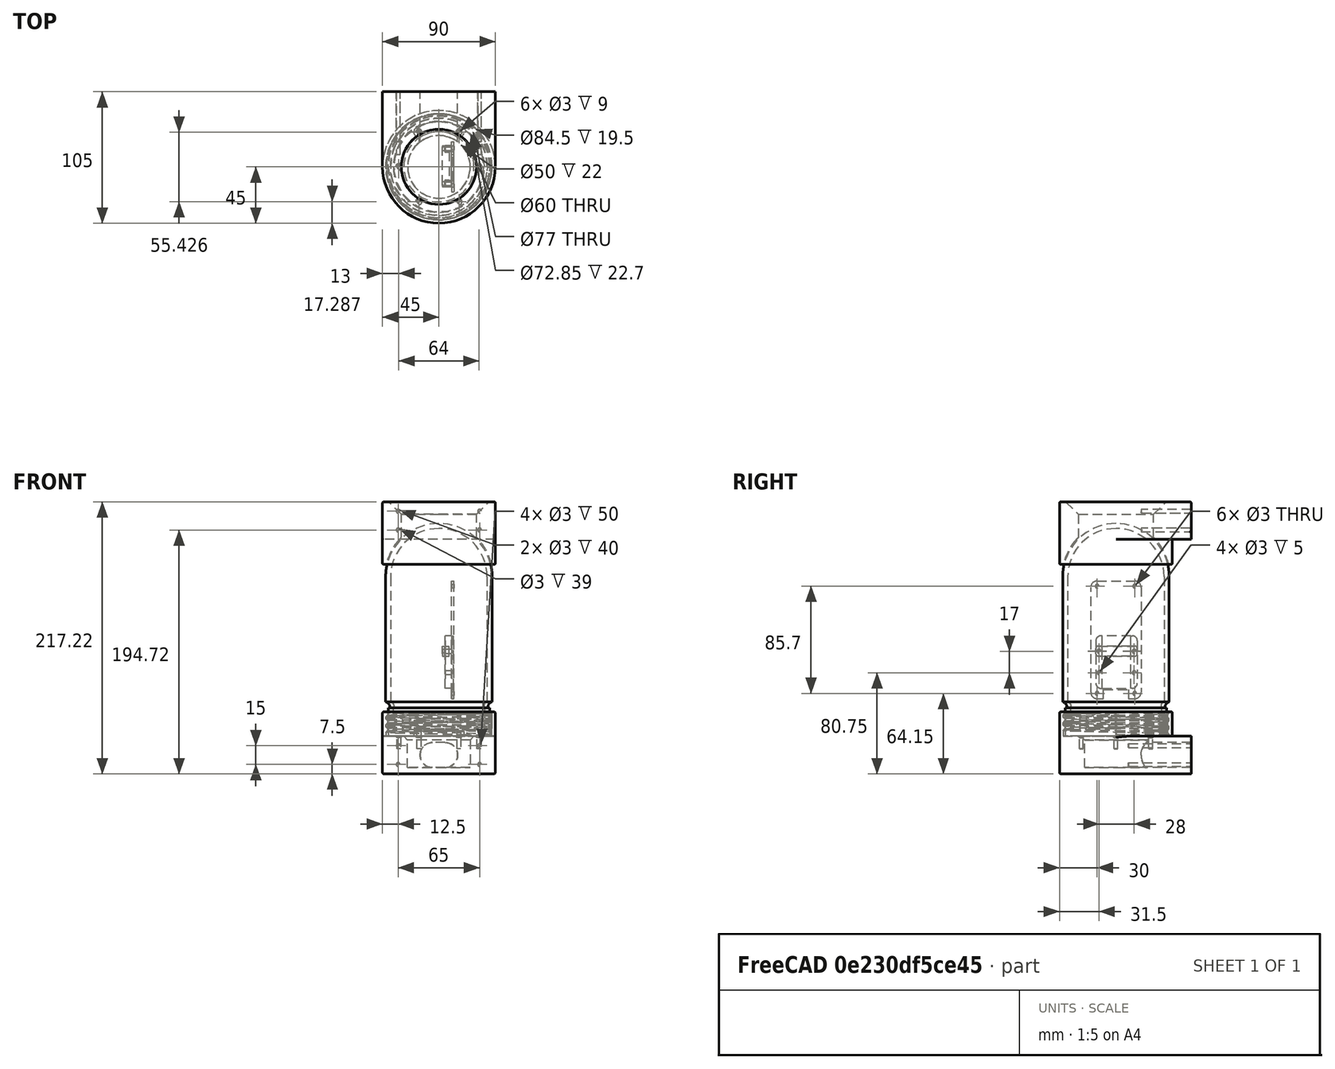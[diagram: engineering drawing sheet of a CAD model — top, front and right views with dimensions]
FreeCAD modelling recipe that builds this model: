
FCSTD DOCUMENT  (FreeCAD 0.19R)
Label: CrocSaintGerard_V4
License: All rights reserved
LicenseURL: http://en.wikipedia.org/wiki/All_rights_reserved
objects: Sketcher::SketchObject×31, PartDesign::Pocket×14, PartDesign::Pad×13, PartDesign::Fillet×11, PartDesign::Body×10, PartDesign::Chamfer×4, PartDesign::Revolution×2, Mesh::Feature×2, Part::Helix×1, PartDesign::ShapeBinder×1, PartDesign::AdditivePipe×1, PartDesign::LinearPattern×1, PartDesign::Groove×1, App::VRMLObject×1
note: 136 computed .brp shape members not serialized (recipe doc carries the construction recipe); baked Part::Feature solids carry a one-line shape summary decoded from their .brp

FEATURE [Part::Helix] Helix
  Angle = 0
  AttacherType = Attacher::AttachEngine3D
  Height = 6.22
  LocalCoord = 0
  Pitch = 6.23
  Radius = 40.5
  Style = 1
FEATURE [Sketcher::SketchObject] Sketch001  label="sketch_cylindre_base"
  FullyConstrained = true
  MapMode = 5
  Support = -> [XY_Plane]
  sketch-geometry (2):
    g0: Circle CenterX=0 CenterY=0 CenterZ=0 NormalX=0 NormalY=0 NormalZ=1 AngleXU=0 Radius=42.25
    g1: Circle CenterX=0 CenterY=0 CenterZ=0 NormalX=0 NormalY=0 NormalZ=1 AngleXU=0 Radius=45
  constraints (4):
    c: Coincident(g0,g-1)
    c: Coincident(g1,g0)
    c: Radius(g0) = 42.25
    c: Radius(g1) = 45
FEATURE [PartDesign::Pad] Pad  label="cylindre_base"
  Direction = (1,1,1)
  Length = 20
  Length2 = 100
  Profile = -> Sketch001
  Type = 0
FEATURE [Sketcher::SketchObject] Sketch002  label="sketch_profil_dent"
  FullyConstrained = true
  MapMode = 5
  Placement = pos=(0,0,0) rot=(1,0,0;1.5708rad)
  Support = -> [XZ_Plane]
  sketch-geometry (7):
    g0: LineSegment StartX=42.25 StartY=4.40427 StartZ=0 EndX=40.9557 EndY=3.11 EndZ=0
    g1: LineSegment StartX=40.9557 StartY=3.11 StartZ=0 EndX=40.9557 EndY=1.29427 EndZ=0
    g2: LineSegment StartX=40.9557 StartY=1.29427 StartZ=0 EndX=42.25 EndY=0 EndZ=0
    g3: LineSegment StartX=42.25 StartY=4.40427 StartZ=0 EndX=42.25 EndY=6.22 EndZ=0
    g4: LineSegment StartX=42.25 StartY=6.22 StartZ=0 EndX=43.25 EndY=6.22 EndZ=0
    g5: LineSegment StartX=43.25 StartY=6.22 StartZ=0 EndX=43.25 EndY=0 EndZ=0
    g6: LineSegment StartX=43.25 StartY=0 StartZ=0 EndX=42.25 EndY=0 EndZ=0
  constraints (21):
    c: Coincident(g0,g1)
    c: Vertical(g1)
    c: Coincident(g1,g2)
    c: DistanceX(g-2,g2) = 42.25
    c: PointOnObject(g2,g-1)
    c: Coincident(g0,g3)
    c: Vertical(g3)
    c: Coincident(g3,g4)
    c: Horizontal(g4)
    c: Coincident(g4,g5)
    c: PointOnObject(g5,g-1)
    c: Vertical(g5)
    c: Coincident(g5,g6)
    c: Coincident(g6,g2)
    c: DistanceX(g4,g4) = 1
    c: Equal(g3,g1)
    c: Equal(g2,g0)
    c: Angle(g2,g-1) = 0.785398
    c: Equal(g1,g3)
    c: DistanceY(g5,g5) = 6.22
    c: DistanceX(g-2,g0) = 42.25
FEATURE [PartDesign::ShapeBinder] ShapeBinder  label="ShapeBinder-helix"
  Support = -> [Helix]
  TraceSupport = false
FEATURE [PartDesign::AdditivePipe] AdditivePipe  label="filet"
  AuxilleryCurvelinear = true
  AuxillerySpineTangent = false
  BaseFeature = -> Pad
  Binormal = (0,0,0)
  Mode = 2
  Profile = -> Sketch002
  Spine = -> ShapeBinder
  SpineTangent = false
  Transformation = 0
  Transition = 0
FEATURE [PartDesign::LinearPattern] LinearPattern  label="ajout_filets"
  BaseFeature = -> AdditivePipe
  Direction = -> Z_Axis
  Length = 12.46
  Occurrences = 3
  Originals = -> [AdditivePipe]
FEATURE [Sketcher::SketchObject] Sketch003  label="sketch_decoupe_filetage"
  FullyConstrained = true
  MapMode = 5
  Placement = pos=(0,0,0) rot=(1,0,0;1.5708rad)
  Support = -> [XZ_Plane]
  sketch-geometry (4):
    g0: LineSegment StartX=-90 StartY=29.5 StartZ=0 EndX=90 EndY=29.5 EndZ=0
    g1: LineSegment StartX=90 StartY=29.5 StartZ=0 EndX=90 EndY=19.5 EndZ=0
    g2: LineSegment StartX=90 StartY=19.5 StartZ=0 EndX=-90 EndY=19.5 EndZ=0
    g3: LineSegment StartX=-90 StartY=19.5 StartZ=0 EndX=-90 EndY=29.5 EndZ=0
  constraints (11):
    c: Coincident(g0,g1)
    c: Coincident(g1,g2)
    c: Coincident(g2,g3)
    c: Coincident(g3,g0)
    c: Horizontal(g2)
    c: Vertical(g1)
    c: Vertical(g3)
    c: DistanceY(g-1,g1) = 19.5
    c: Symmetric(g0,g0,g-2)
    c: DistanceY(g1,g1) = 10
    c: DistanceX(g0,g0) = 180
FEATURE [PartDesign::Pocket] Pocket  label="decoupe_filetage"
  BaseFeature = -> LinearPattern
  Length = 200
  Length2 = 100
  Midplane = true
  Profile = -> Sketch003
  Type = 0
FEATURE [Sketcher::SketchObject] Sketch008  label="sketch_enceinte_verre"
  FullyConstrained = true
  MapMode = 5
  Support = -> [XY_Plane003]
  sketch-geometry (11):
    g0: ArcOfCircle CenterX=-127.4 CenterY=0 CenterZ=0 NormalX=0 NormalY=0 NormalZ=1 AngleXU=0 Radius=42.5 StartAngle=1.5708 EndAngle=3.14159
    g1: ArcOfCircle CenterX=-127.4 CenterY=0 CenterZ=0 NormalX=0 NormalY=0 NormalZ=1 AngleXU=0 Radius=38.5 StartAngle=1.5708 EndAngle=3.14159
    g2: LineSegment StartX=-127.4 StartY=38.5 StartZ=0 EndX=-27.4 EndY=38.5 EndZ=0
    g3: ArcOfCircle CenterX=-24.2871 CenterY=39.1905 CenterZ=0 NormalX=0 NormalY=0 NormalZ=1 AngleXU=0 Radius=3.18854 StartAngle=3.35987 EndAngle=5.2334
    g4: LineSegment StartX=-22.7 StartY=36.425 StartZ=0 EndX=0 EndY=36.425 EndZ=0
    g5: LineSegment StartX=-127.4 StartY=42.5 StartZ=0 EndX=-27.4 EndY=42.5 EndZ=0
    g6: ArcOfCircle CenterX=-22.7 CenterY=43.802 CenterZ=0 NormalX=0 NormalY=0 NormalZ=1 AngleXU=0 Radius=4.87701 StartAngle=3.41184 EndAngle=4.71239
    g7: LineSegment StartX=-22.7 StartY=38.925 StartZ=0 EndX=-22.7 EndY=40.425 EndZ=0
    g8: LineSegment StartX=-22.7 StartY=40.425 StartZ=0 EndX=0 EndY=40.425 EndZ=0
    g9: LineSegment StartX=0 StartY=40.425 StartZ=0 EndX=0 EndY=36.425 EndZ=0
    g10: LineSegment StartX=-165.9 StartY=4.7e-15 StartZ=0 EndX=-169.9 EndY=5.2e-15 EndZ=0
  constraints (35):
    c: PointOnObject(g0,g-1)
    c: PointOnObject(g0,g-1)
    c: Coincident(g1,g0)
    c: PointOnObject(g1,g-1)
    c: Angle(g1) = 1.5708
    c: Angle(g0) = 1.5708
    c: Tangent(g1,g2) = 1.5708
    c: Coincident(g3,g2)
    c: Coincident(g4,g3)
    c: PointOnObject(g4,g-2)
    c: Horizontal(g4)
    c: Coincident(g5,g0)
    c: Horizontal(g5)
    c: Coincident(g6,g5)
    c: Coincident(g6,g7)
    c: Coincident(g7,g8)
    c: PointOnObject(g8,g-2)
    c: Horizontal(g8)
    c: Coincident(g8,g9)
    c: Coincident(g9,g4)
    c: Coincident(g10,g0)
    c: DistanceX(g10,g10) = 4
    c: Radius(g0) = 42.5
    c: Coincident(g1,g10)
    c: DistanceY(g9,g9) = 4
    c: Perpendicular(g6,g7)
    c: Vertical(g7)
    c: DistanceY(g-1,g4) = 36.425
    c: Equal(g4,g8)
    c: DistanceX(g8,g8) = 22.7
    c: DistanceX(g-2,g5) = -27.4
    c: Equal(g2,g5)
    c: PointOnObject(g3,g6)
    c: DistanceY(g7,g7) = 1.5
    c: DistanceX(g5,g5) = 100
FEATURE [PartDesign::Revolution] Revolution  label="revolution_enceinte_verre"
  AllowMultiFace = false
  Angle = 360
  Axis = (1,0,0)
  Base = (0,0,0)
  Profile = -> Sketch008
  ReferenceAxis = -> Sketch008 [H_Axis]
FEATURE [PartDesign::Body] Body003  label="enceinte_verre"
  Group = -> [Sketch008,Revolution]
  Origin = -> Origin003
  Placement = pos=(-3.8e-15,0,-1.78e-14) rot=(0,1,0;1.5708rad)
  Tip = -> Revolution
FEATURE [Sketcher::SketchObject] Sketch  label="sketch_base"
  ExternalGeometry = -> [Pocket]
  FullyConstrained = true
  MapMode = 5
  Placement = pos=(0,0,0) rot=(1,0,0;3.14159rad)
  Support = -> [Pocket]
  sketch-geometry (4):
    g0: ArcOfCircle CenterX=0 CenterY=0 CenterZ=0 NormalX=0 NormalY=0 NormalZ=1 AngleXU=0 Radius=45 StartAngle=0 EndAngle=3.14159
    g1: LineSegment StartX=-45 StartY=5.5e-15 StartZ=0 EndX=-45 EndY=-60 EndZ=0
    g2: LineSegment StartX=-45 StartY=-60 StartZ=0 EndX=45 EndY=-60 EndZ=0
    g3: LineSegment StartX=45 StartY=-60 StartZ=0 EndX=45 EndY=0 EndZ=0
  constraints (11):
    c: Coincident(g0,g-1)
    c: PointOnObject(g0,g-1)
    c: PointOnObject(g0,g-1)
    c: Tangent(g0,g1) = -1.5708
    c: Coincident(g1,g2)
    c: Horizontal(g2)
    c: Coincident(g2,g3)
    c: Coincident(g3,g0)
    c: Vertical(g3)
    c: Radius(g0) = 45
    c: DistanceY(g1,g1) = 60
FEATURE [PartDesign::Pad] Pad001  label="base"
  BaseFeature = -> Pocket
  Direction = (1,1,1)
  Length = 30
  Length2 = 100
  Profile = -> Sketch
  Type = 0
FEATURE [Sketcher::SketchObject] Sketch009  label="sketch_passage_fils"
  FullyConstrained = true
  MapMode = 5
  Support = -> [Pad001]
  sketch-geometry (1):
    g0: Circle CenterX=0 CenterY=0 CenterZ=0 NormalX=0 NormalY=0 NormalZ=1 AngleXU=0 Radius=25
  constraints (2):
    c: Coincident(g0,g-1)
    c: Radius(g0) = 25
FEATURE [PartDesign::Pocket] Pocket001  label="passage_fils"
  BaseFeature = -> Pad001
  Length = 25
  Length2 = 100
  Profile = -> Sketch009
  Type = 0
FEATURE [Sketcher::SketchObject] Sketch010  label="sketch_passage_fils_vertical"
  ExternalGeometry = -> [Pocket001]
  FullyConstrained = true
  MapMode = 5
  Placement = pos=(0,60,0) rot=(0,0.707107,0.707107;3.14159rad)
  Support = -> [Pocket001]
  sketch-geometry (4):
    g0: ArcOfCircle CenterX=-5 CenterY=-15 CenterZ=0 NormalX=0 NormalY=0 NormalZ=1 AngleXU=0 Radius=10 StartAngle=1.5708 EndAngle=4.71239
    g1: ArcOfCircle CenterX=5 CenterY=-15 CenterZ=0 NormalX=0 NormalY=0 NormalZ=1 AngleXU=0 Radius=10 StartAngle=4.71239 EndAngle=7.85398
    g2: LineSegment StartX=-5 StartY=-25 StartZ=0 EndX=5 EndY=-25 EndZ=0
    g3: LineSegment StartX=-5 StartY=-5 StartZ=0 EndX=5 EndY=-5 EndZ=0
  constraints (9):
    c: Tangent(g0,g3) = 1.5708
    c: Tangent(g0,g2) = -1.5708
    c: Tangent(g2,g1) = -1.5708
    c: Tangent(g3,g1) = 1.5708
    c: Equal(g0,g1)
    c: Symmetric(g0,g1,g-2)
    c: Distance(g1,g-3) = 5
    c: DistanceY(g-1,g1) = -5
    c: DistanceX(g2,g2) = 10
FEATURE [PartDesign::Pocket] Pocket002  label="passage_fils_vertical"
  BaseFeature = -> Pocket001
  Length = 60
  Length2 = 100
  Profile = -> Sketch010
  Type = 0
FEATURE [Sketcher::SketchObject] Sketch011  label="sketch_vis_fixation"
  ExternalGeometry = -> [Pocket002]
  FullyConstrained = true
  MapMode = 5
  Placement = pos=(0,60,0) rot=(0,0.707107,0.707107;3.14159rad)
  Support = -> [Pocket002]
  sketch-geometry (4):
    g0: Circle CenterX=-32.5 CenterY=-7.5 CenterZ=0 NormalX=0 NormalY=0 NormalZ=1 AngleXU=0 Radius=1.5
    g1: Circle CenterX=32.5 CenterY=-7.5 CenterZ=0 NormalX=0 NormalY=0 NormalZ=1 AngleXU=0 Radius=1.5
    g2: Circle CenterX=-32.5 CenterY=-22.5 CenterZ=0 NormalX=0 NormalY=0 NormalZ=1 AngleXU=0 Radius=1.5
    g3: Circle CenterX=32.5 CenterY=-22.5 CenterZ=0 NormalX=0 NormalY=0 NormalZ=1 AngleXU=0 Radius=1.5
  constraints (10):
    c: Symmetric(g1,g0,g-2)
    c: DistanceY(g-1,g0) = -7.5
    c: Distance(g0,g1) = 65
    c: Radius(g0) = 1.5
    c: Equal(g0,g1)
    c: Symmetric(g3,g2,g-2)
    c: Radius(g2) = 1.5
    c: Equal(g2,g3)
    c: Distance(g3,g2) = 65
    c: Distance(g3,g-3) = 7.5
FEATURE [PartDesign::Pocket] Pocket003  label="vis_fixation"
  BaseFeature = -> Pocket002
  Length = 50
  Length2 = 100
  Profile = -> Sketch011
  Type = 0
FEATURE [PartDesign::Chamfer] Chamfer
  Angle = 45
  Base = -> Pocket003 [Edge95]
  BaseFeature = -> Pocket003
  ChamferType = 0
  FlipDirection = false
  Size = 3
  Size2 = 1
  SupportTransform = false
FEATURE [Sketcher::SketchObject] Sketch012  label="sketch_vis_montage_interieur"
  FullyConstrained = true
  MapMode = 5
  Support = -> [Chamfer]
  sketch-geometry (13):
    g0: LineSegment StartX=-16 StartY=27.7128 StartZ=0 EndX=-32 EndY=-3.3857e-12 EndZ=0
    g1: LineSegment StartX=-32 StartY=-3.3857e-12 StartZ=0 EndX=-16 EndY=-27.7128 EndZ=0
    g2: LineSegment StartX=-16 StartY=-27.7128 StartZ=0 EndX=16 EndY=-27.7128 EndZ=0
    g3: LineSegment StartX=16 StartY=-27.7128 StartZ=0 EndX=32 EndY=9.738e-12 EndZ=0
    g4: LineSegment StartX=32 StartY=9.738e-12 StartZ=0 EndX=16 EndY=27.7128 EndZ=0
    g5: LineSegment StartX=16 StartY=27.7128 StartZ=0 EndX=-16 EndY=27.7128 EndZ=0
    g6: Circle CenterX=0 CenterY=0 CenterZ=0 NormalX=0 NormalY=0 NormalZ=1 AngleXU=0 Radius=32
    g7: Circle CenterX=-16 CenterY=27.7128 CenterZ=0 NormalX=0 NormalY=0 NormalZ=1 AngleXU=0 Radius=1.5
    g8: Circle CenterX=16 CenterY=27.7128 CenterZ=0 NormalX=0 NormalY=0 NormalZ=1 AngleXU=0 Radius=1.5
    g9: Circle CenterX=-32 CenterY=-3.3857e-12 CenterZ=0 NormalX=0 NormalY=0 NormalZ=1 AngleXU=0 Radius=1.5
    g10: Circle CenterX=32 CenterY=9.738e-12 CenterZ=0 NormalX=0 NormalY=0 NormalZ=1 AngleXU=0 Radius=1.5
    g11: Circle CenterX=16 CenterY=-27.7128 CenterZ=0 NormalX=0 NormalY=0 NormalZ=1 AngleXU=0 Radius=1.5
    g12: Circle CenterX=-16 CenterY=-27.7128 CenterZ=0 NormalX=0 NormalY=0 NormalZ=1 AngleXU=0 Radius=1.5
  constraints (28):
    c: Coincident(g0,g1)
    c: Coincident(g1,g2)
    c: Coincident(g2,g3)
    c: Coincident(g3,g4)
    c: Coincident(g4,g5)
    c: Coincident(g5,g0)
    c: Equal(g0, g1-g5) x5
    c: PointOnObject(g0,g6)
    c: PointOnObject(g1,g6)
    c: PointOnObject(g2,g6)
    c: PointOnObject(g3,g6)
    c: PointOnObject(g4,g6)
    c: PointOnObject(g5,g6)
    c: Coincident(g6,g-1)
    c: Horizontal(g5)
    c: Radius(g6) = 32
    c: Coincident(g7,g0)
    c: Coincident(g8,g4)
    c: Coincident(g9,g0)
    c: Coincident(g10,g3)
    c: Coincident(g11,g2)
    c: Coincident(g12,g1)
    c: Radius(g11) = 1.5
    c: Equal(g11,g12)
    c: Equal(g11,g9)
    c: Equal(g11,g7)
    c: Equal(g11,g8)
    c: Equal(g11,g10)
FEATURE [PartDesign::Pocket] Pocket004  label="vis_montage_interieur"
  BaseFeature = -> Chamfer
  Length = 10
  Length2 = 100
  Profile = -> Sketch012
  Type = 0
FEATURE [PartDesign::Chamfer] Chamfer001
  Angle = 45
  Base = -> Pocket004 [Edge3,Edge2,Edge4,Edge6,Edge8,Edge7]
  BaseFeature = -> Pocket004
  ChamferType = 0
  FlipDirection = false
  Size = 1
  Size2 = 1
  SupportTransform = false
FEATURE [Mesh::Feature] Mesh  label="fixation_enceinte_verre (Meshed)"
FEATURE [Sketcher::SketchObject] Sketch013
  FullyConstrained = true
  MapMode = 5
  Placement = pos=(0,0,0) rot=(0.57735,0.57735,0.57735;2.0944rad)
  Support = -> [YZ_Plane004]
  sketch-geometry (4):
    g0: ArcOfCircle CenterX=0 CenterY=128 CenterZ=0 NormalX=0 NormalY=0 NormalZ=1 AngleXU=0 Radius=43 StartAngle=2.39448 EndAngle=2.92551
    g1: LineSegment StartX=-42 StartY=137.22 StartZ=0 EndX=-45 EndY=137.22 EndZ=0
    g2: LineSegment StartX=-45 StartY=137.22 StartZ=0 EndX=-45 EndY=157.22 EndZ=0
    g3: LineSegment StartX=-45 StartY=157.22 StartZ=0 EndX=-31.5471 EndY=157.22 EndZ=0
  constraints (13):
    c: PointOnObject(g0,g-2)
    c: Coincident(g0,g1)
    c: Coincident(g1,g2)
    c: Vertical(g2)
    c: Coincident(g2,g3)
    c: Coincident(g3,g0)
    c: Horizontal(g3)
    c: Horizontal(g1)
    c: Radius(g0) = 43
    c: DistanceY(g2,g2) = 20
    c: DistanceX(g-2,g1) = -45
    c: DistanceY(g-1,g0) = 128
    c: DistanceX(g1,g1) = 3
FEATURE [PartDesign::Revolution] Revolution001
  Angle = 360
  Axis = (-2e-16,3e-16,1)
  Base = (0,0,0)
  Placement = pos=(0,0,0) rot=(0.57735,0.57735,0.57735;2.0944rad)
  Profile = -> Sketch013
  ReferenceAxis = -> Sketch013 [V_Axis]
FEATURE [Sketcher::SketchObject] Sketch014
  ExternalGeometry = -> [Revolution001]
  FullyConstrained = true
  MapMode = 5
  Placement = pos=(-8.73e-14,6.11e-14,157.22) rot=(0,0,-1;1.5708rad)
  Support = -> [Revolution001]
  sketch-geometry (4):
    g0: ArcOfCircle CenterX=0 CenterY=0 CenterZ=0 NormalX=0 NormalY=0 NormalZ=1 AngleXU=0 Radius=45 StartAngle=4.71239 EndAngle=7.85398
    g1: LineSegment StartX=1.38e-14 StartY=45 StartZ=0 EndX=-60 EndY=45 EndZ=0
    g2: LineSegment StartX=-60 StartY=45 StartZ=0 EndX=-60 EndY=-45 EndZ=0
    g3: LineSegment StartX=-60 StartY=-45 StartZ=0 EndX=-7.1e-15 EndY=-45 EndZ=0
  constraints (10):
    c: Coincident(g0,g-1)
    c: PointOnObject(g0,g-3)
    c: PointOnObject(g0,g-2)
    c: PointOnObject(g0,g-2)
    c: Tangent(g0,g1) = -1.5708
    c: Coincident(g1,g2)
    c: Coincident(g2,g3)
    c: Coincident(g3,g0)
    c: Symmetric(g2,g1,g-1)
    c: DistanceX(g-2,g1) = -60
FEATURE [PartDesign::Pad] Pad002
  BaseFeature = -> Revolution001
  Direction = (1,1,1)
  Length = 30
  Length2 = 100
  Placement = pos=(0,0,0) rot=(0.57735,0.57735,0.57735;2.0944rad)
  Profile = -> Sketch014
  Type = 0
FEATURE [Sketcher::SketchObject] Sketch015
  ExternalGeometry = -> [Pad002]
  FullyConstrained = true
  MapMode = 5
  Placement = pos=(0,0,0) rot=(0.57735,0.57735,0.57735;2.0944rad)
  Support = -> [YZ_Plane004]
  sketch-geometry (3):
    g0: ArcOfCircle CenterX=2.84e-14 CenterY=128 CenterZ=0 NormalX=0 NormalY=0 NormalZ=1 AngleXU=0 Radius=43 StartAngle=1.5708 EndAngle=2.39448
    g1: LineSegment StartX=-31.5471 StartY=157.22 StartZ=0 EndX=3.6e-15 EndY=157.22 EndZ=0
    g2: LineSegment StartX=3.6e-15 StartY=157.22 StartZ=0 EndX=3.6e-15 EndY=171 EndZ=0
  constraints (8):
    c: Coincident(g0,g-3)
    c: Coincident(g0,g-3)
    c: PointOnObject(g0,g-2)
    c: Coincident(g0,g1)
    c: Coincident(g1,g2)
    c: Coincident(g2,g0)
    c: Vertical(g2)
    c: Horizontal(g1)
FEATURE [PartDesign::Groove] Groove
  Angle = 360
  Axis = (-2e-16,3e-16,1)
  Base = (0,0,0)
  BaseFeature = -> Pad002
  Placement = pos=(0,0,0) rot=(0.57735,0.57735,0.57735;2.0944rad)
  Profile = -> Sketch015
  ReferenceAxis = -> Sketch015 [V_Axis]
  Reversed = true
FEATURE [PartDesign::Fillet] Fillet
  Base = -> Chamfer001 [Edge116,Edge168,Edge182,Edge171,Edge181,Edge166]
  BaseFeature = -> Chamfer001
  Radius = 1
  SupportTransform = false
FEATURE [PartDesign::Body] Body  label="fixation_enceinte_verre"
  Group = -> [Sketch001,Pad,Sketch002,ShapeBinder,AdditivePipe,LinearPattern,Sketch003,Pocket,Sketch,Pad001,Sketch009,Pocket001,Sketch010,Pocket002,Sketch011,Pocket003,Chamfer,Sketch012,Pocket004,Chamfer001,Fillet]
  Origin = -> Origin
  Tip = -> Fillet
FEATURE [Sketcher::SketchObject] Sketch019
  FullyConstrained = true
  MapMode = 5
  Support = -> [XY_Plane005]
  sketch-geometry (4):
    g0: ArcOfCircle CenterX=-1.9e-15 CenterY=0 CenterZ=0 NormalX=0 NormalY=0 NormalZ=1 AngleXU=0 Radius=28 StartAngle=1.0472 EndAngle=2.0944
    g1: ArcOfCircle CenterX=-1.9e-15 CenterY=0 CenterZ=0 NormalX=0 NormalY=0 NormalZ=1 AngleXU=0 Radius=36 StartAngle=1.0472 EndAngle=2.0944
    g2: ArcOfCircle CenterX=-16 CenterY=27.7128 CenterZ=0 NormalX=0 NormalY=0 NormalZ=1 AngleXU=0 Radius=4 StartAngle=2.0944 EndAngle=5.23599
    g3: ArcOfCircle CenterX=16 CenterY=27.7128 CenterZ=0 NormalX=0 NormalY=0 NormalZ=1 AngleXU=0 Radius=4 StartAngle=4.18879 EndAngle=7.33038
  constraints (11):
    c: Symmetric(g0,g0,g-2)
    c: Coincident(g1,g0)
    c: Symmetric(g1,g1,g-2)
    c: Coincident(g3,g1)
    c: Tangent(g2,g0) = 1.5708
    c: Tangent(g2,g1) = -1.5708
    c: Tangent(g3,g0) = 1.5708
    c: Coincident(g0,g-1)
    c: Radius(g1) = 36
    c: Radius(g0) = 28
    c: Angle(g0) = 1.0472
FEATURE [PartDesign::Pad] Pad003
  Direction = (1,1,1)
  Length = 4
  Length2 = 100
  Profile = -> Sketch019
  Type = 0
FEATURE [Sketcher::SketchObject] Sketch020
  ExternalGeometry = -> [Pad003]
  FullyConstrained = true
  MapMode = 5
  Placement = pos=(0,0,4) rot=(0,0,1;0rad)
  Support = -> [Pad003]
  sketch-geometry (2):
    g0: Circle CenterX=-16 CenterY=27.7128 CenterZ=0 NormalX=0 NormalY=0 NormalZ=1 AngleXU=0 Radius=1.5
    g1: Circle CenterX=16 CenterY=27.7128 CenterZ=0 NormalX=0 NormalY=0 NormalZ=1 AngleXU=0 Radius=1.5
  constraints (4):
    c: Coincident(g0,g-3)
    c: Coincident(g1,g-4)
    c: Radius(g1) = 1.5
    c: Equal(g1,g0)
FEATURE [PartDesign::Pocket] Pocket008
  BaseFeature = -> Pad003
  Length = 5
  Length2 = 100
  Profile = -> Sketch020
  Type = 0
FEATURE [PartDesign::Body] Body005  label="support_interieur"
  Group = -> [Sketch019,Pad003,Sketch020,Pocket008]
  Origin = -> Origin005
  Tip = -> Pocket008
FEATURE [Sketcher::SketchObject] Sketch021
  FullyConstrained = true
  MapMode = 5
  Placement = pos=(-1.806e-13,1.028e-13,187.22) rot=(0,0,-1;1.5708rad)
  Support = -> [Pad002]
  sketch-geometry (1):
    g0: Circle CenterX=0 CenterY=0 CenterZ=0 NormalX=0 NormalY=0 NormalZ=1 AngleXU=0 Radius=30
  constraints (2):
    c: Coincident(g0,g-1)
    c: Radius(g0) = 30
FEATURE [PartDesign::Pocket] Pocket009
  BaseFeature = -> Groove
  Length = 46
  Length2 = 100
  Placement = pos=(0,0,0) rot=(0.57735,0.57735,0.57735;2.0944rad)
  Profile = -> Sketch021
  Type = 0
FEATURE [Sketcher::SketchObject] Sketch022
  FullyConstrained = false
  MapMode = 5
  Placement = pos=(2.66e-14,60,-6.99e-14) rot=(0.57735,0.57735,0.57735;4.18879rad)
  sketch-geometry (4):
    g0: Circle CenterX=164.72 CenterY=32.5 CenterZ=0 NormalX=0 NormalY=0 NormalZ=1 AngleXU=0 Radius=1.5
    g1: Circle CenterX=179.72 CenterY=32.5 CenterZ=0 NormalX=0 NormalY=0 NormalZ=1 AngleXU=0 Radius=1.5
    g2: Circle CenterX=164.72 CenterY=-32.5 CenterZ=0 NormalX=0 NormalY=0 NormalZ=1 AngleXU=0 Radius=1.5
    g3: Circle CenterX=179.72 CenterY=-32.5 CenterZ=0 NormalX=0 NormalY=0 NormalZ=1 AngleXU=0 Radius=1.5
  constraints (8):
    c: Symmetric(g3,g1,g-1)
    c: Symmetric(g0,g2,g-1)
    c: Distance(g0,g2) = 65
    c: Distance(g3,g1) = 65
    c: Radius(g0) = 1.5
    c: Equal(g0,g1)
    c: Equal(g0,g2)
    c: Equal(g0,g3)
FEATURE [PartDesign::Pocket] Pocket010
  BaseFeature = -> Pocket009
  Length = 40
  Length2 = 100
  Placement = pos=(0,0,0) rot=(0.57735,0.57735,0.57735;2.0944rad)
  Profile = -> Sketch022
  Type = 0
FEATURE [PartDesign::Fillet] Fillet001
  Base = -> Pocket010 [Edge10,Edge27]
  BaseFeature = -> Pocket010
  Placement = pos=(0,0,0) rot=(0.57735,0.57735,0.57735;2.0944rad)
  Radius = 1
  SupportTransform = false
FEATURE [PartDesign::Fillet] Fillet002
  Base = -> Fillet001 [Edge5,Edge21]
  BaseFeature = -> Fillet001
  Placement = pos=(0,0,0) rot=(0.57735,0.57735,0.57735;2.0944rad)
  Radius = 1
  SupportTransform = false
FEATURE [PartDesign::Chamfer] Chamfer002
  Angle = 45
  Base = -> Fillet002 [Edge19]
  BaseFeature = -> Fillet002
  ChamferType = 0
  FlipDirection = false
  Placement = pos=(0,0,0) rot=(0.57735,0.57735,0.57735;2.0944rad)
  Size = 10
  Size2 = 1
  SupportTransform = false
FEATURE [PartDesign::Fillet] Fillet003
  Base = -> Chamfer002 [Edge2]
  BaseFeature = -> Chamfer002
  Placement = pos=(0,0,0) rot=(0.57735,0.57735,0.57735;2.0944rad)
  Radius = 1
  SupportTransform = false
FEATURE [PartDesign::Fillet] Fillet004
  Base = -> Fillet003 [Edge46,Edge5,Edge34]
  BaseFeature = -> Fillet003
  Placement = pos=(0,0,0) rot=(0.57735,0.57735,0.57735;2.0944rad)
  Radius = 1
  SupportTransform = false
FEATURE [PartDesign::Body] Body004  label="tete"
  Group = -> [Sketch013,Revolution001,Sketch014,Pad002,Sketch015,Groove,Sketch021,Pocket009,Sketch022,Pocket010,Fillet001,Fillet002,Chamfer002,Fillet003,Fillet004]
  Origin = -> Origin004
  Tip = -> Fillet004
FEATURE [Mesh::Feature] Mesh001  label="tete (Meshed)"
FEATURE [Sketcher::SketchObject] Sketch005
  FullyConstrained = false
  MapMode = 5
  Placement = pos=(0,0,0) rot=(0.57735,0.57735,0.57735;2.0944rad)
  Support = -> [YZ_Plane002]
  sketch-geometry (8):
    g0: LineSegment StartX=-17 StartY=-5 StartZ=0 EndX=-11.875 EndY=-5 EndZ=0
    g1: LineSegment StartX=-11.875 StartY=-5 StartZ=0 EndX=-11.875 EndY=-1.6 EndZ=0
    g2: LineSegment StartX=-11.875 StartY=-1.6 StartZ=0 EndX=10.875 EndY=-1.6 EndZ=0
    g3: LineSegment StartX=10.875 StartY=-1.6 StartZ=0 EndX=10.875 EndY=-5 EndZ=0
    g4: LineSegment StartX=10.875 StartY=-5 StartZ=0 EndX=16 EndY=-5 EndZ=0
    g5: LineSegment StartX=16 StartY=-5 StartZ=0 EndX=16 EndY=-7 EndZ=0
    g6: LineSegment StartX=16 StartY=-7 StartZ=0 EndX=-17 EndY=-7 EndZ=0
    g7: LineSegment StartX=-17 StartY=-7 StartZ=0 EndX=-17 EndY=-5 EndZ=0
  constraints (24):
    c: Horizontal(g0)
    c: Coincident(g0,g1)
    c: Vertical(g1)
    c: Coincident(g1,g2)
    c: Horizontal(g2)
    c: Coincident(g2,g3)
    c: Vertical(g3)
    c: Coincident(g3,g4)
    c: Horizontal(g4)
    c: Coincident(g4,g5)
    c: Vertical(g5)
    c: Coincident(g5,g6)
    c: Horizontal(g6)
    c: Coincident(g6,g7)
    c: Coincident(g7,g0)
    c: Vertical(g7)
    c: DistanceY(g7,g7) = 2
    c: DistanceY(g1,g1) = 3.4
    c: DistanceX(g2,g2) = 22.75
    c: DistanceX(g0,g0) = 5.125
    c: Equal(g0,g4)
    c: Equal(g5,g7)
    c: DistanceY(g-1,g0) = -5
    c: DistanceX(g-2,g6) = -17
FEATURE [PartDesign::Pad] Pad010
  AllowMultiFace = false
  Direction = (1,1,1)
  Length = 8
  Length2 = 100
  Placement = pos=(0,0,0) rot=(0.57735,0.57735,0.57735;2.0944rad)
  Profile = -> Sketch005
  Type = 0
FEATURE [Sketcher::SketchObject] Sketch006
  ExternalGeometry = -> [Pad010]
  FullyConstrained = true
  MapMode = 5
  Placement = pos=(2.7e-15,-3.9e-15,-7) rot=(0.707107,0.707107,0;3.14159rad)
  Support = -> [Pad010]
  sketch-geometry (2):
    g0: Circle CenterX=-14.5 CenterY=4 CenterZ=0 NormalX=0 NormalY=0 NormalZ=1 AngleXU=0 Radius=1.5
    g1: Circle CenterX=13.5 CenterY=4 CenterZ=0 NormalX=0 NormalY=0 NormalZ=1 AngleXU=0 Radius=1.5
  constraints (6):
    c: Radius(g1) = 1.5
    c: Equal(g1,g0)
    c: DistanceY(g-1,g1) = 4
    c: DistanceY(g-1,g0) = 4
    c: Distance(g0,g-3) = 2.5
    c: Distance(g1,g-4) = 2.5
FEATURE [PartDesign::Pocket] Pocket013
  AllowMultiFace = false
  BaseFeature = -> Pad010
  Length = 5
  Length2 = 100
  Placement = pos=(0,0,0) rot=(0.57735,0.57735,0.57735;2.0944rad)
  Profile = -> Sketch006
  Type = 0
FEATURE [PartDesign::Fillet] Fillet007
  Base = -> Pocket013 [Edge8,Edge7,Edge19,Edge13]
  BaseFeature = -> Pocket013
  Placement = pos=(0,0,0) rot=(0.57735,0.57735,0.57735;2.0944rad)
  Radius = 2
  SupportTransform = false
FEATURE [PartDesign::Body] Body002  label="Attache"
  Group = -> [Sketch005,Pad010,Sketch006,Pocket013,Fillet007]
  Origin = -> Origin002
  Placement = pos=(9.75,-3.1e-15,64) rot=(-0.707107,0,-0.707107;3.14159rad)
  Tip = -> Fillet007
FEATURE [App::VRMLObject] CroqueLivreSaintGerard2021_V1
  Placement = pos=(0,0,0) rot=(1,0,0;3.14159rad)
  Resources = CroqueLivreSaintGerard2021_V1/CP_Radial_D12.5mm_P5.00mm.wrl | CroqueLivreSaintGerard2021_V1/ | CroqueLivreSaintGerard2021_V1/ | CroqueLivreSaintGerard2021_V1/ | CroqueLivreSaintGerard2021_V1/ | CroqueLivreSaintGerard2021_V1/ | CroqueLivreSaintGerard2021_V1/ | CroqueLivreSaintGerard2021_V1/ | CroqueLivreSaintGerard2021_V1/ | CroqueLivreSaintGerard2021_V1/ | CroqueLivreSaintGerard2021_V1/ | CroqueLivreSaintGerard2021_V1/
FEATURE [Sketcher::SketchObject] Sketch025
  FullyConstrained = true
  MapMode = 5
  Support = -> [XY_Plane006]
  sketch-geometry (17):
    g0: LineSegment StartX=-47 StartY=20 StartZ=0 EndX=47 EndY=20 EndZ=0
    g1: LineSegment StartX=47 StartY=20 StartZ=0 EndX=47 EndY=-20 EndZ=0
    g2: LineSegment StartX=47 StartY=-20 StartZ=0 EndX=-47 EndY=-20 EndZ=0
    g3: LineSegment StartX=-39.75 StartY=18.75 StartZ=0 EndX=39.75 EndY=18.75 EndZ=0
    g4: LineSegment StartX=39.75 StartY=18.75 StartZ=0 EndX=39.75 EndY=-18.75 EndZ=0
    g5: LineSegment StartX=39.75 StartY=-18.75 StartZ=0 EndX=-39.75 EndY=-18.75 EndZ=0
    g6: LineSegment StartX=-39.75 StartY=-18.75 StartZ=0 EndX=-39.75 EndY=18.75 EndZ=0
    g7: Circle CenterX=-42.85 CenterY=15 CenterZ=0 NormalX=0 NormalY=0 NormalZ=1 AngleXU=0 Radius=1.5
    g8: Circle CenterX=-42.85 CenterY=-15 CenterZ=0 NormalX=0 NormalY=0 NormalZ=1 AngleXU=0 Radius=1.5
    g9: Circle CenterX=42.85 CenterY=-15 CenterZ=0 NormalX=0 NormalY=0 NormalZ=1 AngleXU=0 Radius=1.5
    g10: Circle CenterX=42.85 CenterY=15 CenterZ=0 NormalX=0 NormalY=0 NormalZ=1 AngleXU=0 Radius=1.5
    g11: Circle CenterX=-42.85 CenterY=15 CenterZ=0 NormalX=0 NormalY=0 NormalZ=1 AngleXU=0 Radius=3
    g12: LineSegment StartX=-47 StartY=20 StartZ=0 EndX=-47 EndY=10 EndZ=0
    g13: LineSegment StartX=-47 StartY=10 StartZ=0 EndX=-39.75 EndY=10 EndZ=0
    g14: LineSegment StartX=-39.75 StartY=10 StartZ=0 EndX=-39.75 EndY=-10 EndZ=0
    g15: LineSegment StartX=-39.75 StartY=-10 StartZ=0 EndX=-47 EndY=-10 EndZ=0
    g16: LineSegment StartX=-47 StartY=-10 StartZ=0 EndX=-47 EndY=-20 EndZ=0
  constraints (44):
    c: Coincident(g0,g1)
    c: Coincident(g1,g2)
    c: Horizontal(g0)
    c: Horizontal(g2)
    c: Vertical(g1)
    c: Symmetric(g0,g1,g-1)
    c: DistanceY(g1,g1) = 40
    c: DistanceX(g0,g0) = 94
    c: Coincident(g3,g4)
    c: Coincident(g4,g5)
    c: Coincident(g5,g6)
    c: Coincident(g6,g3)
    c: Horizontal(g3)
    c: Horizontal(g5)
    c: Vertical(g4)
    c: Vertical(g6)
    c: Symmetric(g3,g4,g-1)
    c: DistanceY(g6,g6) = 37.5
    c: DistanceX(g3,g3) = 79.5
    c: Radius(g10) = 1.5
    c: Equal(g10,g9)
    c: Equal(g10,g8)
    c: Equal(g10,g7)
    c: Symmetric(g7,g8,g-1)
    c: Symmetric(g10,g9,g-1)
    c: Symmetric(g10,g7,g-2)
    c: Coincident(g11,g7)
    c: Radius(g11) = 3
    c: Coincident(g0,g12)
    c: Vertical(g12)
    c: Coincident(g12,g13)
    c: Horizontal(g13)
    c: Coincident(g13,g14)
    c: Vertical(g14)
    c: Coincident(g14,g15)
    c: Horizontal(g15)
    c: Coincident(g15,g16)
    c: Coincident(g16,g2)
    c: Vertical(g16)
    c: Symmetric(g15,g12,g-1)
    c: PointOnObject(g13,g6)
    c: DistanceY(g14,g14) = 20
    c: DistanceY(g-1,g7) = 15
    c: DistanceX(g-2,g7) = -42.85
FEATURE [PartDesign::Pad] Pad011
  AllowMultiFace = false
  Direction = (1,1,1)
  Length = 2
  Length2 = 100
  Profile = -> Sketch025
  Type = 0
FEATURE [PartDesign::Fillet] Fillet006
  Base = -> Pad011 [Edge8,Edge5,Edge11,Edge1]
  BaseFeature = -> Pad011
  Radius = 5
  SupportTransform = false
FEATURE [Sketcher::SketchObject] Sketch024
  ExternalGeometry = -> [Fillet006]
  FullyConstrained = true
  MapMode = 5
  Placement = pos=(0,0,0) rot=(1,0,0;3.14159rad)
  Support = -> [Fillet006]
  sketch-geometry (4):
    g0: LineSegment StartX=-38.75 StartY=12 StartZ=0 EndX=3.25 EndY=12 EndZ=0
    g1: LineSegment StartX=3.25 StartY=12 StartZ=0 EndX=3.25 EndY=-11 EndZ=0
    g2: LineSegment StartX=3.25 StartY=-11 StartZ=0 EndX=-38.75 EndY=-11 EndZ=0
    g3: LineSegment StartX=-38.75 StartY=-11 StartZ=0 EndX=-38.75 EndY=12 EndZ=0
  constraints (12):
    c: Coincident(g0,g1)
    c: Coincident(g1,g2)
    c: Coincident(g2,g3)
    c: Coincident(g3,g0)
    c: Horizontal(g0)
    c: Horizontal(g2)
    c: Vertical(g1)
    c: Vertical(g3)
    c: DistanceY(g1,g1) = 23
    c: DistanceX(g0,g0) = 42
    c: DistanceY(g-1,g0) = 12
    c: Distance(g0,g-3) = 1
FEATURE [PartDesign::Pocket] Pocket012
  AllowMultiFace = false
  BaseFeature = -> Fillet006
  Length = 1.5
  Length2 = 100
  Profile = -> Sketch024
  Type = 0
FEATURE [Sketcher::SketchObject] Sketch026
  FullyConstrained = true
  MapMode = 5
  Support = -> [XY_Plane001]
  sketch-geometry (16):
    g0: LineSegment StartX=-47 StartY=20 StartZ=0 EndX=47 EndY=20 EndZ=0
    g1: LineSegment StartX=47 StartY=20 StartZ=0 EndX=47 EndY=-20 EndZ=0
    g2: LineSegment StartX=47 StartY=-20 StartZ=0 EndX=-47 EndY=-20 EndZ=0
    g3: LineSegment StartX=-47 StartY=-20 StartZ=0 EndX=-47 EndY=20 EndZ=0
    g4: Circle CenterX=-42.85 CenterY=15 CenterZ=0 NormalX=0 NormalY=0 NormalZ=1 AngleXU=0 Radius=1.5
    g5: Circle CenterX=-42.85 CenterY=-15 CenterZ=0 NormalX=0 NormalY=0 NormalZ=1 AngleXU=0 Radius=1.5
    g6: Circle CenterX=42.85 CenterY=15 CenterZ=0 NormalX=0 NormalY=0 NormalZ=1 AngleXU=0 Radius=1.5
    g7: Circle CenterX=42.85 CenterY=-15 CenterZ=0 NormalX=0 NormalY=0 NormalZ=1 AngleXU=0 Radius=1.5
    g8: LineSegment StartX=-32.25 StartY=15.5 StartZ=0 EndX=37.75 EndY=15.5 EndZ=0
    g9: LineSegment StartX=37.75 StartY=15.5 StartZ=0 EndX=37.75 EndY=-15.5 EndZ=0
    g10: LineSegment StartX=37.75 StartY=-15.5 StartZ=0 EndX=-32.25 EndY=-15.5 EndZ=0
    g11: LineSegment StartX=-32.25 StartY=-15.5 StartZ=0 EndX=-32.25 EndY=15.5 EndZ=0
    g12: LineSegment StartX=-39.75 StartY=18.75 StartZ=0 EndX=39.75 EndY=18.75 EndZ=0
    g13: LineSegment StartX=39.75 StartY=18.75 StartZ=0 EndX=39.75 EndY=-18.75 EndZ=0
    g14: LineSegment StartX=39.75 StartY=-18.75 StartZ=0 EndX=-39.75 EndY=-18.75 EndZ=0
    g15: LineSegment StartX=-39.75 StartY=-18.75 StartZ=0 EndX=-39.75 EndY=18.75 EndZ=0
  constraints (42):
    c: Coincident(g0,g1)
    c: Coincident(g1,g2)
    c: Coincident(g2,g3)
    c: Coincident(g3,g0)
    c: Horizontal(g0)
    c: Horizontal(g2)
    c: Vertical(g1)
    c: Vertical(g3)
    c: Symmetric(g1,g0,g-1)
    c: DistanceX(g0,g0) = 94
    c: DistanceY(g3,g3) = 40
    c: Radius(g4) = 1.5
    c: Equal(g4,g6)
    c: Equal(g4,g5)
    c: Equal(g4,g7)
    c: Symmetric(g5,g4,g-1)
    c: Symmetric(g6,g7,g-1)
    c: Symmetric(g4,g6,g-2)
    c: DistanceY(g-1,g4) = 15
    c: DistanceX(g-2,g4) = -42.85
    c: Coincident(g8,g9)
    c: Coincident(g9,g10)
    c: Coincident(g10,g11)
    c: Coincident(g11,g8)
    c: Horizontal(g8)
    c: Horizontal(g10)
    c: Vertical(g11)
    c: DistanceY(g9,g9) = 31
    c: DistanceX(g8,g8) = 70
    c: Symmetric(g8,g9,g-1)
    c: Coincident(g12,g13)
    c: Coincident(g13,g14)
    c: Coincident(g14,g15)
    c: Coincident(g15,g12)
    c: Horizontal(g12)
    c: Horizontal(g14)
    c: Vertical(g13)
    c: Vertical(g15)
    c: DistanceX(g12,g12) = 79.5
    c: Symmetric(g12,g13,g-1)
    c: DistanceY(g15,g15) = 37.5
    c: Distance(g8,g13) = 2
FEATURE [PartDesign::Pad] Pad009
  AllowMultiFace = false
  Direction = (1,1,1)
  Length = 3
  Length2 = 100
  Profile = -> Sketch026
  Type = 0
FEATURE [Sketcher::SketchObject] Sketch023
  FullyConstrained = true
  MapMode = 5
  Placement = pos=(0,0,0) rot=(1,0,0;3.14159rad)
  Support = -> [Pad009]
  sketch-geometry (4):
    g0: LineSegment StartX=-39.75 StartY=18.75 StartZ=0 EndX=39.75 EndY=18.75 EndZ=0
    g1: LineSegment StartX=39.75 StartY=18.75 StartZ=0 EndX=39.75 EndY=-18.75 EndZ=0
    g2: LineSegment StartX=39.75 StartY=-18.75 StartZ=0 EndX=-39.75 EndY=-18.75 EndZ=0
    g3: LineSegment StartX=-39.75 StartY=-18.75 StartZ=0 EndX=-39.75 EndY=18.75 EndZ=0
  constraints (11):
    c: Coincident(g0,g1)
    c: Coincident(g1,g2)
    c: Coincident(g2,g3)
    c: Coincident(g3,g0)
    c: Horizontal(g0)
    c: Horizontal(g2)
    c: Vertical(g1)
    c: Vertical(g3)
    c: DistanceY(g1,g1) = 37.5
    c: DistanceX(g0,g0) = 79.5
    c: Symmetric(g0,g2,g-1)
FEATURE [PartDesign::Pocket] Pocket011
  AllowMultiFace = false
  BaseFeature = -> Pad009
  Length = 1.5
  Length2 = 100
  Profile = -> Sketch023
  Type = 0
FEATURE [PartDesign::Fillet] Fillet005
  Base = -> Pocket011 [Edge5,Edge1,Edge8,Edge2]
  BaseFeature = -> Pocket011
  Radius = 5
  SupportTransform = false
FEATURE [PartDesign::Chamfer] Chamfer003
  Angle = 45
  Base = -> Fillet005 [Edge33,Edge34,Edge35,Edge36]
  BaseFeature = -> Fillet005
  ChamferType = 0
  FlipDirection = false
  Size = 2
  Size2 = 1
  SupportTransform = false
FEATURE [PartDesign::Body] Body001  label="Devant"
  Group = -> [Sketch026,Pad009,Sketch023,Pocket011,Fillet005,Chamfer003]
  Origin = -> Origin001
  Placement = pos=(12,-3.4e-15,77) rot=(-0.707107,0,-0.707107;3.14159rad)
  Tip = -> Chamfer003
FEATURE [Sketcher::SketchObject] Sketch027
  FullyConstrained = false
  MapMode = 5
  Support = -> [XY_Plane007]
  sketch-geometry (32):
    g0: LineSegment StartX=-42.5 StartY=27.5 StartZ=0 EndX=-50.5 EndY=27.5 EndZ=0
    g1: LineSegment StartX=-50.5 StartY=27.5 StartZ=0 EndX=-50.5 EndY=-27.5 EndZ=0
    g2: LineSegment StartX=-50.5 StartY=-27.5 StartZ=0 EndX=-42.5 EndY=-27.5 EndZ=0
    g3: LineSegment StartX=-39.35 StartY=-19.2718 StartZ=0 EndX=-39.35 EndY=-11.2718 EndZ=0
    g4: LineSegment StartX=-39.35 StartY=-11.2718 StartZ=0 EndX=-45.5 EndY=-11.2718 EndZ=0
    g5: LineSegment StartX=-45.5 StartY=-11.2718 StartZ=0 EndX=-45.5 EndY=11.2718 EndZ=0
    g6: LineSegment StartX=-45.5 StartY=11.2718 StartZ=0 EndX=-39.35 EndY=11.2718 EndZ=0
    g7: LineSegment StartX=-39.35 StartY=11.2718 StartZ=0 EndX=-39.35 EndY=19.2718 EndZ=0
    g8: Circle CenterX=-46.5 CenterY=23.05 CenterZ=0 NormalX=0 NormalY=0 NormalZ=1 AngleXU=0 Radius=1.5
    g9: Circle CenterX=-46.5 CenterY=-23.05 CenterZ=0 NormalX=0 NormalY=0 NormalZ=1 AngleXU=0 Radius=1.5
    g10: Circle CenterX=-42.85 CenterY=15 CenterZ=0 NormalX=0 NormalY=0 NormalZ=1 AngleXU=0 Radius=1.5
    g11: Circle CenterX=-42.85 CenterY=-15 CenterZ=0 NormalX=0 NormalY=0 NormalZ=1 AngleXU=0 Radius=1.5
    g12: LineSegment StartX=49.755 StartY=30.8637 StartZ=0 EndX=49.755 EndY=-30.8637 EndZ=0
    g13: LineSegment StartX=49.755 StartY=-30.8637 StartZ=0 EndX=41.755 EndY=-30.8637 EndZ=0
    g14: LineSegment StartX=41.755 StartY=-30.8637 StartZ=0 EndX=41.755 EndY=-38.5255 EndZ=0
    g15: LineSegment StartX=41.755 StartY=-38.5255 StartZ=0 EndX=-42.5 EndY=-38.5255 EndZ=0
    g16: LineSegment StartX=-42.5 StartY=-38.5255 StartZ=0 EndX=-42.5 EndY=-27.5 EndZ=0
    g17: LineSegment StartX=-42.2511 StartY=27.3386 StartZ=0 EndX=-42.2511 EndY=32.1776 EndZ=0
    g18: LineSegment StartX=-42.2511 StartY=32.1776 StartZ=0 EndX=41.755 EndY=32.1776 EndZ=0
    g19: LineSegment StartX=41.755 StartY=32.1776 StartZ=0 EndX=41.755 EndY=30.8637 EndZ=0
    g20: LineSegment StartX=41.755 StartY=30.8637 StartZ=0 EndX=49.755 EndY=30.8637 EndZ=0
    g21: Circle CenterX=45.755 CenterY=23.05 CenterZ=0 NormalX=0 NormalY=0 NormalZ=1 AngleXU=0 Radius=1.5
    g22: Circle CenterX=45.755 CenterY=-23.05 CenterZ=0 NormalX=0 NormalY=0 NormalZ=1 AngleXU=0 Radius=1.5
    g23: Circle CenterX=42.85 CenterY=-15 CenterZ=0 NormalX=0 NormalY=0 NormalZ=1 AngleXU=0 Radius=1.5
    g24: Circle CenterX=42.85 CenterY=15 CenterZ=0 NormalX=0 NormalY=0 NormalZ=1 AngleXU=0 Radius=1.5
    g25: LineSegment StartX=-39.35 StartY=19.2718 StartZ=0 EndX=37.8374 EndY=19.2718 EndZ=0
    g26: LineSegment StartX=37.8374 StartY=19.2718 StartZ=0 EndX=37.8374 EndY=10.1343 EndZ=0
    g27: LineSegment StartX=37.8374 StartY=10.1343 StartZ=0 EndX=44.0206 EndY=10.1343 EndZ=0
    g28: LineSegment StartX=44.0206 StartY=10.1343 StartZ=0 EndX=44.0206 EndY=-10.4318 EndZ=0
    g29: LineSegment StartX=44.0206 StartY=-10.4318 StartZ=0 EndX=37.9718 EndY=-10.4318 EndZ=0
    g30: LineSegment StartX=37.9718 StartY=-10.4318 StartZ=0 EndX=37.9718 EndY=-19.2718 EndZ=0
    g31: LineSegment StartX=37.9718 StartY=-19.2718 StartZ=0 EndX=-39.35 EndY=-19.2718 EndZ=0
  constraints (77):
    c: Horizontal(g0)
    c: Coincident(g0,g1)
    c: Vertical(g1)
    c: Coincident(g1,g2)
    c: Horizontal(g2)
    c: Vertical(g3)
    c: Coincident(g3,g4)
    c: Horizontal(g4)
    c: Coincident(g4,g5)
    c: Coincident(g5,g6)
    c: Horizontal(g6)
    c: Coincident(g6,g7)
    c: Vertical(g7)
    c: Symmetric(g2,g0,g-1)
    c: Symmetric(g7,g3,g-1)
    c: Symmetric(g4,g5,g-1)
    c: DistanceX(g-2,g0) = -50.5
    c: DistanceX(g0,g0) = 8
    c: DistanceY(g7,g7) = 8
    c: Distance(g5,g1) = 5
    c: Radius(g9) = 1.5
    c: Equal(g9,g8)
    c: Distance(g8,g9) = 46.1
    c: Symmetric(g8,g9,g-1)
    c: Distance(g9,g1) = 4
    c: Symmetric(g11,g10,g-1)
    c: Radius(g10) = 1.5
    c: Equal(g10,g11)
    c: Distance(g10,g7) = 3.5
    c: DistanceX(g-2,g10) = -42.85
    c: DistanceY(g1,g1) = 55
    c: DistanceY(g-1,g10) = 15
    c: Vertical(g12)
    c: Coincident(g12,g13)
    c: Horizontal(g13)
    c: Coincident(g13,g14)
    c: Vertical(g14)
    c: Coincident(g14,g15)
    c: Horizontal(g15)
    c: Coincident(g15,g16)
    c: Coincident(g16,g2)
    c: Vertical(g17)
    c: Coincident(g17,g18)
    c: Horizontal(g18)
    c: Coincident(g18,g19)
    c: Vertical(g19)
    c: Coincident(g19,g20)
    c: Coincident(g20,g12)
    c: Horizontal(g20)
    c: Equal(g20,g13)
    c: DistanceX(g20,g20) = 8
    c: Radius(g21) = 1.5
    c: Equal(g21,g24)
    c: Equal(g21,g23)
    c: Equal(g21,g22)
    c: Symmetric(g24,g23,g-1)
    c: Symmetric(g21,g22,g-1)
    c: Distance(g22,g21) = 46.1
    c: Distance(g24,g23) = 30
    c: Distance(g21,g12) = 4
    c: Vertical(g16)
    c: DistanceX(g-2,g24) = 42.85
    c: Symmetric(g13,g19,g-1)
    c: Coincident(g7,g25)
    c: Horizontal(g25)
    c: Coincident(g25,g26)
    c: Vertical(g26)
    c: Coincident(g26,g27)
    c: Horizontal(g27)
    c: Coincident(g27,g28)
    c: Vertical(g28)
    c: Coincident(g28,g29)
    c: Horizontal(g29)
    c: Coincident(g29,g30)
    c: Vertical(g30)
    c: Coincident(g30,g31)
    c: Horizontal(g31)
FEATURE [PartDesign::Pad] Pad006
  Direction = (1,1,1)
  Length = 10
  Length2 = 100
  Profile = -> Sketch027
  Type = 0
FEATURE [Sketcher::SketchObject] Sketch028
  ExternalGeometry = -> [Pad006]
  FullyConstrained = true
  MapMode = 5
  Placement = pos=(-50.5,0,0) rot=(0.57735,-0.57735,-0.57735;2.0944rad)
  Support = -> [Pad006]
  sketch-geometry (4):
    g0: LineSegment StartX=-10 StartY=10 StartZ=0 EndX=10 EndY=10 EndZ=0
    g1: LineSegment StartX=10 StartY=10 StartZ=0 EndX=10 EndY=5 EndZ=0
    g2: LineSegment StartX=10 StartY=5 StartZ=0 EndX=-10 EndY=5 EndZ=0
    g3: LineSegment StartX=-10 StartY=5 StartZ=0 EndX=-10 EndY=10 EndZ=0
  constraints (11):
    c: Coincident(g0,g1)
    c: Coincident(g1,g2)
    c: Coincident(g2,g3)
    c: Coincident(g3,g0)
    c: Horizontal(g2)
    c: Vertical(g1)
    c: Vertical(g3)
    c: DistanceY(g3,g3) = 5
    c: Symmetric(g0,g0,g-2)
    c: DistanceX(g0,g0) = 20
    c: PointOnObject(g0,g-3)
FEATURE [PartDesign::Pocket] Pocket014
  BaseFeature = -> Pad006
  Length = 6
  Length2 = 100
  Profile = -> Sketch028
  Type = 0
FEATURE [Sketcher::SketchObject] Sketch029
  ExternalGeometry = -> [Pocket014]
  FullyConstrained = true
  MapMode = 5
  Placement = pos=(0,0,0) rot=(1,0,0;3.14159rad)
  Support = -> [Pocket014]
  sketch-geometry (10):
    g0: Circle CenterX=-46.5 CenterY=-23.05 CenterZ=0 NormalX=0 NormalY=0 NormalZ=1 AngleXU=0 Radius=1.5
    g1: Circle CenterX=-46.5 CenterY=23.05 CenterZ=0 NormalX=0 NormalY=0 NormalZ=1 AngleXU=0 Radius=1.5
    g2: LineSegment StartX=-50.5 StartY=27.5 StartZ=0 EndX=-42.5 EndY=27.5 EndZ=0
    g3: LineSegment StartX=-42.5 StartY=27.5 StartZ=0 EndX=-42.5 EndY=19 EndZ=0
    g4: LineSegment StartX=-42.5 StartY=19 StartZ=0 EndX=-50.5 EndY=19 EndZ=0
    g5: LineSegment StartX=-50.5 StartY=19 StartZ=0 EndX=-50.5 EndY=27.5 EndZ=0
    g6: LineSegment StartX=-42.5 StartY=-19 StartZ=0 EndX=-50.5 EndY=-19 EndZ=0
    g7: LineSegment StartX=-50.5 StartY=-19 StartZ=0 EndX=-50.5 EndY=-27.5 EndZ=0
    g8: LineSegment StartX=-50.5 StartY=-27.5 StartZ=0 EndX=-42.5 EndY=-27.5 EndZ=0
    g9: LineSegment StartX=-42.5 StartY=-27.5 StartZ=0 EndX=-42.5 EndY=-19 EndZ=0
  constraints (27):
    c: Radius(g1) = 1.5
    c: Equal(g1,g0)
    c: Coincident(g2,g3)
    c: Coincident(g3,g4)
    c: Coincident(g4,g5)
    c: Coincident(g5,g2)
    c: Horizontal(g2)
    c: Horizontal(g4)
    c: Vertical(g3)
    c: Vertical(g5)
    c: Coincident(g6,g7)
    c: Coincident(g7,g8)
    c: Coincident(g8,g9)
    c: Coincident(g9,g6)
    c: Horizontal(g6)
    c: Horizontal(g8)
    c: Vertical(g7)
    c: Vertical(g9)
    c: DistanceX(g2,g2) = 8
    c: Equal(g8,g2)
    c: Distance(g1,g5) = 4
    c: Distance(g1,g2) = 4.45
    c: Equal(g7,g5)
    c: Symmetric(g0,g1,g-1)
    c: Coincident(g2,g-3)
    c: Coincident(g7,g-3)
    c: PointOnObject(g3,g-4)
FEATURE [PartDesign::Pad] Pad007
  BaseFeature = -> Pocket014
  Direction = (1,1,1)
  Length = 15
  Length2 = 100
  Profile = -> Sketch029
  Type = 0
FEATURE [Sketcher::SketchObject] Sketch030
  ExternalGeometry = -> [Pocket012]
  FullyConstrained = true
  MapMode = 5
  Placement = pos=(0,0,0) rot=(1,0,0;3.14159rad)
  Support = -> [Pocket012]
  sketch-geometry (12):
    g0: LineSegment StartX=-38.75 StartY=12 StartZ=0 EndX=3.25 EndY=12 EndZ=0
    g1: LineSegment StartX=3.25 StartY=12 StartZ=0 EndX=3.25 EndY=17 EndZ=0
    g2: LineSegment StartX=3.25 StartY=17 StartZ=0 EndX=-38.75 EndY=17 EndZ=0
    g3: LineSegment StartX=-38.75 StartY=17 StartZ=0 EndX=-38.75 EndY=12 EndZ=0
    g4: LineSegment StartX=-38.75 StartY=-11 StartZ=0 EndX=3.25 EndY=-11 EndZ=0
    g5: LineSegment StartX=3.25 StartY=-11 StartZ=0 EndX=3.25 EndY=-16 EndZ=0
    g6: LineSegment StartX=3.25 StartY=-16 StartZ=0 EndX=-38.75 EndY=-16 EndZ=0
    g7: LineSegment StartX=-38.75 StartY=-16 StartZ=0 EndX=-38.75 EndY=-11 EndZ=0
    g8: Circle CenterX=-26.25 CenterY=14.5 CenterZ=0 NormalX=0 NormalY=0 NormalZ=1 AngleXU=0 Radius=1.5
    g9: Circle CenterX=-26.25 CenterY=-13.5 CenterZ=0 NormalX=0 NormalY=0 NormalZ=1 AngleXU=0 Radius=1.5
    g10: Circle CenterX=-9.25 CenterY=14.5 CenterZ=0 NormalX=0 NormalY=0 NormalZ=1 AngleXU=0 Radius=1.5
    g11: Circle CenterX=-9.25 CenterY=-13.5 CenterZ=0 NormalX=0 NormalY=0 NormalZ=1 AngleXU=0 Radius=1.5
  constraints (32):
    c: Coincident(g0,g1)
    c: Coincident(g1,g2)
    c: Coincident(g2,g3)
    c: Coincident(g3,g0)
    c: Horizontal(g2)
    c: Vertical(g1)
    c: Vertical(g3)
    c: Coincident(g0,g-3)
    c: Coincident(g4,g5)
    c: Coincident(g5,g6)
    c: Coincident(g6,g7)
    c: Coincident(g7,g4)
    c: Horizontal(g6)
    c: Vertical(g5)
    c: Vertical(g7)
    c: Coincident(g4,g-4)
    c: Coincident(g4,g-4)
    c: Coincident(g0,g-3)
    c: Equal(g1,g5)
    c: DistanceY(g1,g1) = 5
    c: Radius(g11) = 1.5
    c: Equal(g11,g10)
    c: Equal(g11,g8)
    c: Equal(g11,g9)
    c: Distance(g8,g0) = 2.5
    c: Distance(g10,g0) = 2.5
    c: Distance(g8,g3) = 12.5
    c: Distance(g10,g1) = 12.5
    c: Distance(g9,g4) = 2.5
    c: Distance(g11,g4) = 2.5
    c: Distance(g9,g7) = 12.5
    c: Distance(g11,g5) = 12.5
FEATURE [PartDesign::Pad] Pad008
  BaseFeature = -> Pocket012
  Direction = (1,1,1)
  Length = 5
  Length2 = 100
  Profile = -> Sketch030
  Type = 0
FEATURE [PartDesign::Fillet] Fillet008
  Base = -> Pad008 [Edge55,Edge68,Edge58,Edge66]
  BaseFeature = -> Pad008
  Radius = 4
  SupportTransform = false
FEATURE [PartDesign::Body] Body006  label="Plaque"
  Group = -> [Sketch025,Pad011,Fillet006,Sketch024,Pocket012,Sketch030,Pad008,Fillet008]
  Origin = -> Origin008
  Placement = pos=(10,-3.1e-15,77) rot=(-0.707107,0,-0.707107;3.14159rad)
  Tip = -> Fillet008
FEATURE [PartDesign::Fillet] Fillet010
  Base = -> Pad007 [Edge17,Edge44]
  BaseFeature = -> Pad007
  Radius = 4
  SupportTransform = false
FEATURE [PartDesign::Body] Body007  label="Support_ecran_PCB"
  Group = -> [Sketch027,Pad006,Sketch028,Pocket014,Sketch029,Pad007,Fillet010]
  Origin = -> Origin006
  Placement = pos=(-1.9e-14,-9e-16,77) rot=(-0.707107,0,-0.707107;3.14159rad)
  Tip = -> Fillet010
FEATURE [Sketcher::SketchObject] Sketch033
  FullyConstrained = true
  MapMode = 5
  Support = -> [XY_Plane008]
  sketch-geometry (16):
    g0: LineSegment StartX=-42.5 StartY=27.5 StartZ=0 EndX=-50.5 EndY=27.5 EndZ=0
    g1: LineSegment StartX=-50.5 StartY=27.5 StartZ=0 EndX=-50.5 EndY=-27.5 EndZ=0
    g2: LineSegment StartX=-50.5 StartY=-27.5 StartZ=0 EndX=-42.5 EndY=-27.5 EndZ=0
    g3: LineSegment StartX=-42.5 StartY=-27.5 StartZ=0 EndX=-42.5 EndY=-19 EndZ=0
    g4: LineSegment StartX=-42.5 StartY=-19 StartZ=0 EndX=-39.35 EndY=-19 EndZ=0
    g5: LineSegment StartX=-39.35 StartY=-19 StartZ=0 EndX=-39.35 EndY=-11 EndZ=0
    g6: LineSegment StartX=-39.35 StartY=-11 StartZ=0 EndX=-45.5 EndY=-11 EndZ=0
    g7: LineSegment StartX=-45.5 StartY=-11 StartZ=0 EndX=-45.5 EndY=11 EndZ=0
    g8: LineSegment StartX=-45.5 StartY=11 StartZ=0 EndX=-39.35 EndY=11 EndZ=0
    g9: LineSegment StartX=-39.35 StartY=11 StartZ=0 EndX=-39.35 EndY=19 EndZ=0
    g10: LineSegment StartX=-39.35 StartY=19 StartZ=0 EndX=-42.5 EndY=19 EndZ=0
    g11: LineSegment StartX=-42.5 StartY=19 StartZ=0 EndX=-42.5 EndY=27.5 EndZ=0
    g12: Circle CenterX=-46.5 CenterY=23.05 CenterZ=0 NormalX=0 NormalY=0 NormalZ=1 AngleXU=0 Radius=1.5
    g13: Circle CenterX=-46.5 CenterY=-23.05 CenterZ=0 NormalX=0 NormalY=0 NormalZ=1 AngleXU=0 Radius=1.5
    g14: Circle CenterX=-42.85 CenterY=15 CenterZ=0 NormalX=0 NormalY=0 NormalZ=1 AngleXU=0 Radius=1.5
    g15: Circle CenterX=-42.85 CenterY=-15 CenterZ=0 NormalX=0 NormalY=0 NormalZ=1 AngleXU=0 Radius=1.5
  constraints (43):
    c: Horizontal(g0)
    c: Coincident(g0,g1)
    c: Vertical(g1)
    c: Coincident(g1,g2)
    c: Horizontal(g2)
    c: Coincident(g2,g3)
    c: Vertical(g3)
    c: Coincident(g3,g4)
    c: Coincident(g4,g5)
    c: Vertical(g5)
    c: Coincident(g5,g6)
    c: Horizontal(g6)
    c: Coincident(g6,g7)
    c: Coincident(g7,g8)
    c: Horizontal(g8)
    c: Coincident(g8,g9)
    c: Vertical(g9)
    c: Coincident(g9,g10)
    c: Coincident(g10,g11)
    c: Coincident(g11,g0)
    c: Vertical(g11)
    c: Symmetric(g2,g0,g-1)
    c: Horizontal(g10)
    c: Symmetric(g9,g4,g-1)
    c: Symmetric(g6,g7,g-1)
    c: Horizontal(g4)
    c: DistanceX(g-2,g0) = -50.5
    c: DistanceX(g0,g0) = 8
    c: DistanceY(g9,g9) = 8
    c: Distance(g7,g1) = 5
    c: Radius(g13) = 1.5
    c: Equal(g13,g12)
    c: Distance(g12,g13) = 46.1
    c: Symmetric(g12,g13,g-1)
    c: Distance(g13,g1) = 4
    c: Symmetric(g15,g14,g-1)
    c: Radius(g14) = 1.5
    c: Equal(g14,g15)
    c: Distance(g14,g9) = 3.5
    c: DistanceX(g-2,g14) = -42.85
    c: DistanceY(g1,g1) = 55
    c: Distance(g14,g10) = 4
    c: DistanceY(g-1,g14) = 15
FEATURE [PartDesign::Pad] Pad012
  Direction = (1,1,1)
  Length = 10
  Length2 = 100
  Profile = -> Sketch033
  Type = 0
FEATURE [Sketcher::SketchObject] Sketch031
  ExternalGeometry = -> [Pad012]
  FullyConstrained = true
  MapMode = 5
  Placement = pos=(-50.5,0,0) rot=(0.57735,-0.57735,-0.57735;2.0944rad)
  Support = -> [Pad012]
  sketch-geometry (4):
    g0: LineSegment StartX=-10 StartY=10 StartZ=0 EndX=10 EndY=10 EndZ=0
    g1: LineSegment StartX=10 StartY=10 StartZ=0 EndX=10 EndY=5 EndZ=0
    g2: LineSegment StartX=10 StartY=5 StartZ=0 EndX=-10 EndY=5 EndZ=0
    g3: LineSegment StartX=-10 StartY=5 StartZ=0 EndX=-10 EndY=10 EndZ=0
  constraints (11):
    c: Coincident(g0,g1)
    c: Coincident(g1,g2)
    c: Coincident(g2,g3)
    c: Coincident(g3,g0)
    c: Horizontal(g2)
    c: Vertical(g1)
    c: Vertical(g3)
    c: DistanceY(g3,g3) = 5
    c: Symmetric(g0,g0,g-2)
    c: DistanceX(g0,g0) = 20
    c: PointOnObject(g0,g-3)
FEATURE [PartDesign::Pocket] Pocket015
  BaseFeature = -> Pad012
  Length = 6
  Length2 = 100
  Profile = -> Sketch031
  Type = 0
FEATURE [Sketcher::SketchObject] Sketch032
  ExternalGeometry = -> [Pocket015]
  FullyConstrained = true
  MapMode = 5
  Placement = pos=(0,0,0) rot=(1,0,0;3.14159rad)
  Support = -> [Pocket015]
  sketch-geometry (10):
    g0: Circle CenterX=-46.5 CenterY=-23.05 CenterZ=0 NormalX=0 NormalY=0 NormalZ=1 AngleXU=0 Radius=1.5
    g1: Circle CenterX=-46.5 CenterY=23.05 CenterZ=0 NormalX=0 NormalY=0 NormalZ=1 AngleXU=0 Radius=1.5
    g2: LineSegment StartX=-50.5 StartY=27.5 StartZ=0 EndX=-42.5 EndY=27.5 EndZ=0
    g3: LineSegment StartX=-42.5 StartY=27.5 StartZ=0 EndX=-42.5 EndY=19 EndZ=0
    g4: LineSegment StartX=-42.5 StartY=19 StartZ=0 EndX=-50.5 EndY=19 EndZ=0
    g5: LineSegment StartX=-50.5 StartY=19 StartZ=0 EndX=-50.5 EndY=27.5 EndZ=0
    g6: LineSegment StartX=-42.5 StartY=-19 StartZ=0 EndX=-50.5 EndY=-19 EndZ=0
    g7: LineSegment StartX=-50.5 StartY=-19 StartZ=0 EndX=-50.5 EndY=-27.5 EndZ=0
    g8: LineSegment StartX=-50.5 StartY=-27.5 StartZ=0 EndX=-42.5 EndY=-27.5 EndZ=0
    g9: LineSegment StartX=-42.5 StartY=-27.5 StartZ=0 EndX=-42.5 EndY=-19 EndZ=0
  constraints (27):
    c: Radius(g1) = 1.5
    c: Equal(g1,g0)
    c: Coincident(g2,g3)
    c: Coincident(g3,g4)
    c: Coincident(g4,g5)
    c: Coincident(g5,g2)
    c: Horizontal(g2)
    c: Horizontal(g4)
    c: Vertical(g3)
    c: Vertical(g5)
    c: Coincident(g6,g7)
    c: Coincident(g7,g8)
    c: Coincident(g8,g9)
    c: Coincident(g9,g6)
    c: Horizontal(g6)
    c: Horizontal(g8)
    c: Vertical(g7)
    c: Vertical(g9)
    c: DistanceX(g2,g2) = 8
    c: Equal(g8,g2)
    c: Distance(g1,g5) = 4
    c: Distance(g1,g2) = 4.45
    c: Equal(g7,g5)
    c: Symmetric(g0,g1,g-1)
    c: Coincident(g2,g-3)
    c: Coincident(g7,g-3)
    c: PointOnObject(g3,g-4)
FEATURE [PartDesign::Pad] Pad013
  BaseFeature = -> Pocket015
  Direction = (1,1,1)
  Length = 15
  Length2 = 100
  Profile = -> Sketch032
  Type = 0
FEATURE [PartDesign::Fillet] Fillet011
  Base = -> Pad013 [Edge17,Edge44]
  BaseFeature = -> Pad013
  Radius = 4
  SupportTransform = false
FEATURE [PartDesign::Body] Body008  label="Support_ecran_PCB001"
  Group = -> [Sketch033,Pad012,Sketch031,Pocket015,Sketch032,Pad013,Fillet011]
  Origin = -> Origin009
  Placement = pos=(-1.9e-14,-1e-15,77) rot=(0,-1,0;4.71239rad)
  Tip = -> Fillet011
FEATURE [Sketcher::SketchObject] Sketch034
  FullyConstrained = true
  MapMode = 5
  Placement = pos=(0,0,0) rot=(0.57735,0.57735,0.57735;2.0944rad)
  Support = -> [YZ_Plane009]
  sketch-geometry (20):
    g0: LineSegment StartX=-27.5 StartY=127.5 StartZ=0 EndX=27.5 EndY=127.5 EndZ=0
    g1: LineSegment StartX=27.5 StartY=26.5 StartZ=0 EndX=-27.5 EndY=26.5 EndZ=0
    g2: LineSegment StartX=-27.5 StartY=127.5 StartZ=0 EndX=-27.5 EndY=119.5 EndZ=0
    g3: LineSegment StartX=-27.5 StartY=119.5 StartZ=0 EndX=-39.5 EndY=119.5 EndZ=0
    g4: LineSegment StartX=-39.5 StartY=119.5 StartZ=0 EndX=-39.5 EndY=34.5 EndZ=0
    g5: LineSegment StartX=-39.5 StartY=34.5 StartZ=0 EndX=-27.5 EndY=34.5 EndZ=0
    g6: LineSegment StartX=-27.5 StartY=34.5 StartZ=0 EndX=-27.5 EndY=26.5 EndZ=0
    g7: LineSegment StartX=27.5 StartY=26.5 StartZ=0 EndX=27.5 EndY=34.5 EndZ=0
    g8: LineSegment StartX=27.5 StartY=34.5 StartZ=0 EndX=39.5 EndY=34.5 EndZ=0
    g9: LineSegment StartX=39.5 StartY=34.5 StartZ=0 EndX=39.5 EndY=119.5 EndZ=0
    g10: LineSegment StartX=39.5 StartY=119.5 StartZ=0 EndX=27.5 EndY=119.5 EndZ=0
    g11: LineSegment StartX=27.5 StartY=119.5 StartZ=0 EndX=27.5 EndY=127.5 EndZ=0
    g12: Circle CenterX=-23 CenterY=123.5 CenterZ=0 NormalX=0 NormalY=0 NormalZ=1 AngleXU=0 Radius=1.5
    g13: Circle CenterX=-15 CenterY=119.85 CenterZ=0 NormalX=0 NormalY=0 NormalZ=1 AngleXU=0 Radius=1.5
    g14: Circle CenterX=15 CenterY=119.85 CenterZ=0 NormalX=0 NormalY=0 NormalZ=1 AngleXU=0 Radius=1.5
    g15: Circle CenterX=23 CenterY=123.5 CenterZ=0 NormalX=0 NormalY=0 NormalZ=1 AngleXU=0 Radius=1.5
    g16: Circle CenterX=-23 CenterY=30.5 CenterZ=0 NormalX=0 NormalY=0 NormalZ=1 AngleXU=0 Radius=1.5
    g17: Circle CenterX=-15 CenterY=34.15 CenterZ=0 NormalX=0 NormalY=0 NormalZ=1 AngleXU=0 Radius=1.5
    g18: Circle CenterX=15 CenterY=34.15 CenterZ=0 NormalX=0 NormalY=0 NormalZ=1 AngleXU=0 Radius=1.5
    g19: Circle CenterX=23 CenterY=30.5 CenterZ=0 NormalX=0 NormalY=0 NormalZ=1 AngleXU=0 Radius=1.5
  constraints (51):
    c: Coincident(g0,g2)
    c: Vertical(g2)
    c: Coincident(g2,g3)
    c: Horizontal(g3)
    c: Coincident(g3,g4)
    c: Vertical(g4)
    c: Coincident(g4,g5)
    c: Horizontal(g5)
    c: Coincident(g5,g6)
    c: Coincident(g6,g1)
    c: Coincident(g1,g7)
    c: Vertical(g7)
    c: Coincident(g7,g8)
    c: Horizontal(g8)
    c: Coincident(g8,g9)
    c: Vertical(g9)
    c: Coincident(g9,g10)
    c: Horizontal(g10)
    c: Coincident(g10,g11)
    c: Coincident(g11,g0)
    c: Vertical(g11)
    c: Symmetric(g0,g0,g-2)
    c: Symmetric(g1,g1,g-2)
    c: Vertical(g6)
    c: Radius(g19) = 1.5
    c: Equal(g19,g18)
    c: Equal(g19,g17)
    c: Equal(g19,g16)
    c: Equal(g19, g12-g15) x4
    c: Symmetric(g12,g15,g-2)
    c: Symmetric(g13,g14,g-2)
    c: Symmetric(g17,g18,g-2)
    c: Symmetric(g16,g19,g-2)
    c: Distance(g17,g18) = 30
    c: Distance(g13,g14) = 30
    c: DistanceY(g-1,g1) = 26.5
    c: Distance(g0,g1) = 101
    c: DistanceX(g1,g1) = 55
    c: Equal(g1,g0)
    c: Distance(g17,g1) = 7.65
    c: Distance(g13,g0) = 7.65
    c: Distance(g12,g0) = 4
    c: DistanceX(g-2,g12) = -23
    c: DistanceX(g-2,g16) = -23
    c: Distance(g16,g1) = 4
    c: Equal(g8,g5)
    c: DistanceY(g11,g11) = 8
    c: Equal(g11,g2)
    c: Equal(g7,g6)
    c: DistanceY(g7,g7) = 8
    c: DistanceX(g10,g10) = 12
FEATURE [PartDesign::Pad] Pad014
  Direction = (1,1,1)
  Length = 10
  Length2 = 100
  Placement = pos=(0,0,0) rot=(0.57735,0.57735,0.57735;2.0944rad)
  Profile = -> Sketch034
  Type = 0
FEATURE [Sketcher::SketchObject] Sketch035
  ExternalGeometry = -> [Pad014]
  FullyConstrained = true
  MapMode = 5
  Placement = pos=(10,-4.4e-15,3.3e-15) rot=(0.57735,0.57735,0.57735;2.0944rad)
  Support = -> [Pad014]
  sketch-geometry (8):
    g0: LineSegment StartX=-18.5 StartY=116.25 StartZ=0 EndX=18.5 EndY=116.25 EndZ=0
    g1: LineSegment StartX=18.5 StartY=116.25 StartZ=0 EndX=18.5 EndY=37.6 EndZ=0
    g2: LineSegment StartX=-18.5 StartY=37.6 StartZ=0 EndX=-18.5 EndY=116.25 EndZ=0
    g3: LineSegment StartX=-18.5 StartY=37.6 StartZ=0 EndX=-11 EndY=37.6 EndZ=0
    g4: LineSegment StartX=-11 StartY=37.6 StartZ=0 EndX=-11 EndY=31.5 EndZ=0
    g5: LineSegment StartX=-11 StartY=31.5 StartZ=0 EndX=11 EndY=31.5 EndZ=0
    g6: LineSegment StartX=11 StartY=31.5 StartZ=0 EndX=11 EndY=37.6 EndZ=0
    g7: LineSegment StartX=11 StartY=37.6 StartZ=0 EndX=18.5 EndY=37.6 EndZ=0
  constraints (22):
    c: Coincident(g0,g1)
    c: Coincident(g2,g0)
    c: Vertical(g1)
    c: Vertical(g2)
    c: Symmetric(g0,g0,g-2)
    c: Distance(g-4,g0) = 3.6
    c: DistanceX(g2,g1) = 37
    c: Coincident(g2,g3)
    c: Horizontal(g3)
    c: Coincident(g3,g4)
    c: Vertical(g4)
    c: Coincident(g4,g5)
    c: Coincident(g5,g6)
    c: Vertical(g6)
    c: Coincident(g6,g7)
    c: Coincident(g7,g1)
    c: Horizontal(g7)
    c: Symmetric(g4,g5,g-2)
    c: DistanceX(g-2,g4) = -11
    c: DistanceY(g-1,g3) = 37.6
    c: Distance(g4,g-5) = 5
    c: DistanceY(g-1,g6) = 37.6
FEATURE [PartDesign::Pocket] Pocket016
  BaseFeature = -> Pad014
  Length = 13
  Length2 = 100
  Placement = pos=(0,0,0) rot=(0.57735,0.57735,0.57735;2.0944rad)
  Profile = -> Sketch035
  Type = 0
FEATURE [PartDesign::Body] Body009  label="Support"
  Group = -> [Sketch034,Pad014,Sketch035,Pocket016]
  Origin = -> Origin010
  Tip = -> Pocket016
